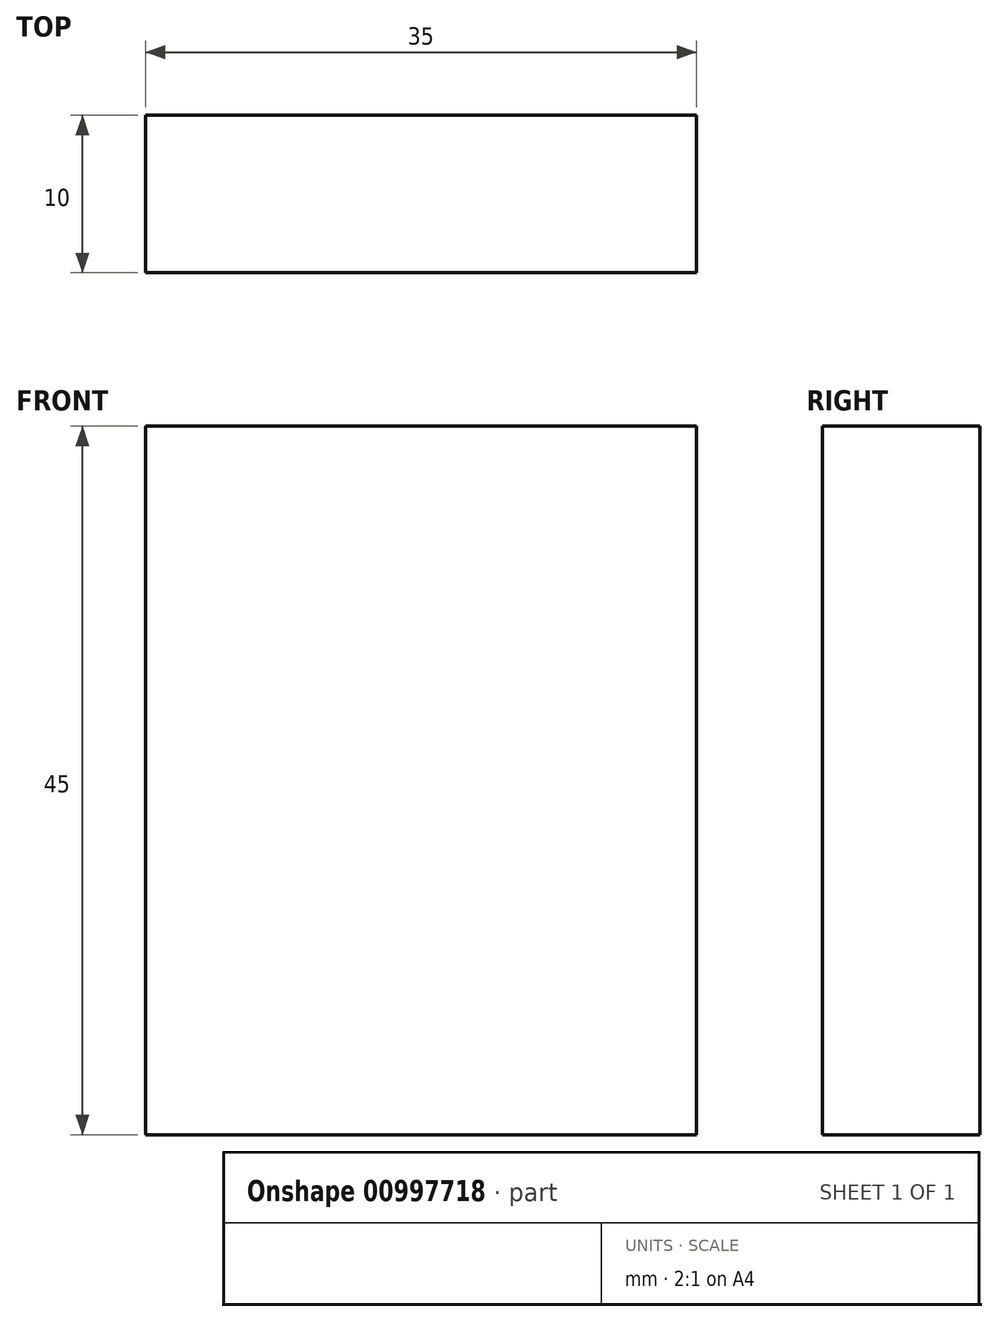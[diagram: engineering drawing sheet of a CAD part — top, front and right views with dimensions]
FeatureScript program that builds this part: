
annotation { "Feature Type Name" : "Feature", "Feature Type Description" : "" }
export const myFeature = defineFeature(function(context is Context, id is Id, definition is map)
    precondition{}
    {
        {
            var Q0;
            Q0=qCreatedBy(makeId("Front.planeOp"),FACE);
            var sketch = newSketch(context, id + "F0", { "sketchPlane" : qUnion([Q0])});
            skLineSegment(sketch, "E0.bottom", {"start": v(0, 0) * mm, "end": v(35, 0) * mm});
            skLineSegment(sketch, "E0.top", {"start": v(0, -45) * mm, "end": v(35, -45) * mm});
            skLineSegment(sketch, "E0.left", {"start": v(0, 0) * mm, "end": v(0, -45) * mm});
            skLineSegment(sketch, "E0.right", {"start": v(35, 0) * mm, "end": v(35, -45) * mm});
            skSolve(sketch);
        }
        {
            var Q0;
            Q0=makeQuery(id+"F0.imprint","IMPRINT",FACE,{"disambiguationData":[TD([[makeQuery(id+"F0.imprint","IMPRINT",EDGE,{"derivedFrom":sQuery(id+"F0.wireOp",EDGE,"E0.bottom")}),-1.0]])]});
            extrude(context, id + "F1", {"entities" : qUnion([Q0]), "depth" : 10 * mm, "offsetDistance" : 25 * mm});
        }
    });
